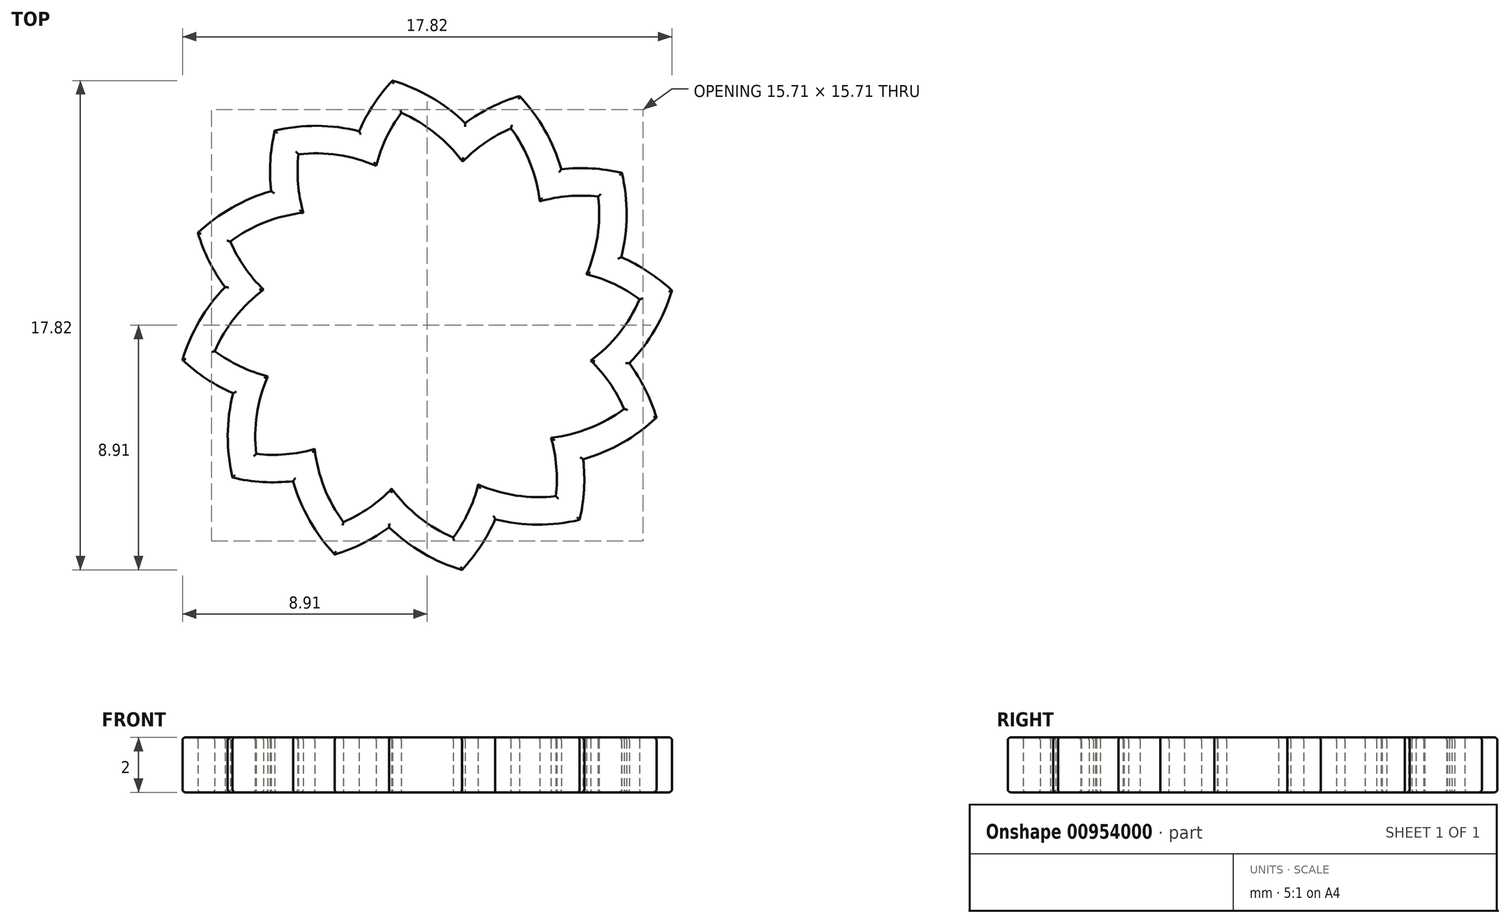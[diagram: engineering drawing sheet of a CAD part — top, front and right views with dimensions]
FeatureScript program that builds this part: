
annotation { "Feature Type Name" : "Feature", "Feature Type Description" : "" }
export const myFeature = defineFeature(function(context is Context, id is Id, definition is map)
    precondition{}
    {
        {
            var Q0;
            Q0=qCreatedBy(makeId("Top.planeOp"),FACE);
            var sketch = newSketch(context, id + "F0", { "sketchPlane" : qUnion([Q0])});
            skCircle(sketch, "E0", {"center": v(0, 0) * mm, "radius": 2.5 * mm});
            skSolve(sketch);
        }
        {
            var Q0;
            Q0=qCreatedBy(makeId("Top.planeOp"),FACE);
            var sketch = newSketch(context, id + "F1", { "sketchPlane" : qUnion([Q0])});
            skArc(sketch, "E1", {"start": v(-2.5, 0) * mm, "mid": v(-5.2, 3.04) * mm, "end": v(-5.55, 7.09) * mm});
            skArc(sketch, "E2", {"start": v(2.43, 0.6) * mm, "mid": v(0.03, 5.81) * mm, "end": v(-5.55, 7.09) * mm});
            skArc(sketch, "E3.1.0", {"start": v(1.8, 1.74) * mm, "mid": v(-2.88, 5.05) * mm, "end": v(-8.35, 3.36) * mm});
            skArc(sketch, "E3.1.1", {"start": v(-2.17, -1.25) * mm, "mid": v(-6.02, 0.04) * mm, "end": v(-8.35, 3.36) * mm});
            skArc(sketch, "E3.2.0", {"start": v(0.69, 2.4) * mm, "mid": v(-5.01, 2.93) * mm, "end": v(-8.91, -1.26) * mm});
            skArc(sketch, "E3.2.1", {"start": v(-1.25, -2.17) * mm, "mid": v(-5.23, -2.98) * mm, "end": v(-8.91, -1.26) * mm});
            skArc(sketch, "E3.3.0", {"start": v(-0.6, 2.43) * mm, "mid": v(-5.81, 0.03) * mm, "end": v(-7.09, -5.55) * mm});
            skArc(sketch, "E3.3.1", {"start": v(0, -2.5) * mm, "mid": v(-3.04, -5.2) * mm, "end": v(-7.09, -5.55) * mm});
            skArc(sketch, "E3.4.0", {"start": v(-1.74, 1.8) * mm, "mid": v(-5.05, -2.88) * mm, "end": v(-3.36, -8.35) * mm});
            skArc(sketch, "E3.4.1", {"start": v(1.25, -2.17) * mm, "mid": v(-0.04, -6.02) * mm, "end": v(-3.36, -8.35) * mm});
            skArc(sketch, "E3.5.0", {"start": v(-2.4, 0.69) * mm, "mid": v(-2.93, -5.01) * mm, "end": v(1.26, -8.91) * mm});
            skArc(sketch, "E3.5.1", {"start": v(2.17, -1.25) * mm, "mid": v(2.98, -5.23) * mm, "end": v(1.26, -8.91) * mm});
            skArc(sketch, "E3.6.0", {"start": v(-2.43, -0.6) * mm, "mid": v(-0.03, -5.81) * mm, "end": v(5.55, -7.09) * mm});
            skArc(sketch, "E3.6.1", {"start": v(2.5, 0) * mm, "mid": v(5.2, -3.04) * mm, "end": v(5.55, -7.09) * mm});
            skArc(sketch, "E3.7.0", {"start": v(-1.8, -1.74) * mm, "mid": v(2.88, -5.05) * mm, "end": v(8.35, -3.36) * mm});
            skArc(sketch, "E3.7.1", {"start": v(2.17, 1.25) * mm, "mid": v(6.02, -0.04) * mm, "end": v(8.35, -3.36) * mm});
            skArc(sketch, "E3.8.0", {"start": v(-0.69, -2.4) * mm, "mid": v(5.01, -2.93) * mm, "end": v(8.91, 1.26) * mm});
            skArc(sketch, "E3.8.1", {"start": v(1.25, 2.17) * mm, "mid": v(5.23, 2.98) * mm, "end": v(8.91, 1.26) * mm});
            skArc(sketch, "E3.9.0", {"start": v(0.6, -2.43) * mm, "mid": v(5.81, -0.03) * mm, "end": v(7.09, 5.55) * mm});
            skArc(sketch, "E3.9.1", {"start": v(0, 2.5) * mm, "mid": v(3.04, 5.2) * mm, "end": v(7.09, 5.55) * mm});
            skPoint(sketch, "E3.center", {"position": v(0, 0) * mm});
            skArc(sketch, "E4.0", {"start": v(0.19, 0.15) * mm, "mid": v(-3.52, 2.17) * mm, "end": v(-4.68, 6.22) * mm});
            skArc(sketch, "E4.1", {"start": v(1.25, 2.17) * mm, "mid": v(-0.96, 5.3) * mm, "end": v(-4.68, 6.22) * mm});
            skArc(sketch, "E5.1.0", {"start": v(0.09, 0.22) * mm, "mid": v(-4.13, 0.12) * mm, "end": v(-7.17, 3.05) * mm});
            skArc(sketch, "E5.1.1", {"start": v(0, 2.5) * mm, "mid": v(-3.48, 4.11) * mm, "end": v(-7.17, 3.05) * mm});
            skArc(sketch, "E5.2.0", {"start": v(-0.04, 0.24) * mm, "mid": v(-3.64, -1.96) * mm, "end": v(-7.73, -0.94) * mm});
            skArc(sketch, "E5.2.1", {"start": v(-1.25, 2.17) * mm, "mid": v(-5.07, 1.82) * mm, "end": v(-7.73, -0.94) * mm});
            skArc(sketch, "E5.3.0", {"start": v(-0.15, 0.19) * mm, "mid": v(-2.17, -3.52) * mm, "end": v(-6.22, -4.68) * mm});
            skArc(sketch, "E5.3.1", {"start": v(-2.17, 1.25) * mm, "mid": v(-5.3, -0.96) * mm, "end": v(-6.22, -4.68) * mm});
            skArc(sketch, "E5.4.0", {"start": v(-0.22, 0.09) * mm, "mid": v(-0.12, -4.13) * mm, "end": v(-3.05, -7.17) * mm});
            skArc(sketch, "E5.4.1", {"start": v(-2.5, 0) * mm, "mid": v(-4.11, -3.48) * mm, "end": v(-3.05, -7.17) * mm});
            skArc(sketch, "E5.5.0", {"start": v(-0.24, -0.04) * mm, "mid": v(1.96, -3.64) * mm, "end": v(0.94, -7.73) * mm});
            skArc(sketch, "E5.5.1", {"start": v(-2.17, -1.25) * mm, "mid": v(-1.82, -5.07) * mm, "end": v(0.94, -7.73) * mm});
            skArc(sketch, "E5.6.0", {"start": v(-0.19, -0.15) * mm, "mid": v(3.52, -2.17) * mm, "end": v(4.68, -6.22) * mm});
            skArc(sketch, "E5.6.1", {"start": v(-1.25, -2.17) * mm, "mid": v(0.96, -5.3) * mm, "end": v(4.68, -6.22) * mm});
            skArc(sketch, "E5.7.0", {"start": v(-0.09, -0.22) * mm, "mid": v(4.13, -0.12) * mm, "end": v(7.17, -3.05) * mm});
            skArc(sketch, "E5.7.1", {"start": v(0, -2.5) * mm, "mid": v(3.48, -4.11) * mm, "end": v(7.17, -3.05) * mm});
            skArc(sketch, "E5.8.0", {"start": v(0.04, -0.24) * mm, "mid": v(3.64, 1.96) * mm, "end": v(7.73, 0.94) * mm});
            skArc(sketch, "E5.8.1", {"start": v(1.25, -2.17) * mm, "mid": v(5.07, -1.82) * mm, "end": v(7.73, 0.94) * mm});
            skArc(sketch, "E5.9.0", {"start": v(0.15, -0.19) * mm, "mid": v(2.17, 3.52) * mm, "end": v(6.22, 4.68) * mm});
            skArc(sketch, "E5.9.1", {"start": v(2.17, -1.25) * mm, "mid": v(5.3, 0.96) * mm, "end": v(6.22, 4.68) * mm});
            skCircle(sketch, "E6", {"center": v(0, 0) * mm, "radius": 2.5 * mm});
            skArc(sketch, "E7.4.10.0", {"start": v(2.5, 0) * mm, "mid": v(4.11, 3.48) * mm, "end": v(3.05, 7.17) * mm});
            skArc(sketch, "E7.5.10.0", {"start": v(0.22, -0.09) * mm, "mid": v(0.12, 4.13) * mm, "end": v(3.05, 7.17) * mm});
            skArc(sketch, "E7.4.11.0", {"start": v(2.17, 1.25) * mm, "mid": v(1.82, 5.07) * mm, "end": v(-0.94, 7.73) * mm});
            skArc(sketch, "E7.5.11.0", {"start": v(0.24, 0.04) * mm, "mid": v(-1.96, 3.64) * mm, "end": v(-0.94, 7.73) * mm});
            skArc(sketch, "E8.1.10.0", {"start": v(1.74, -1.8) * mm, "mid": v(5.05, 2.88) * mm, "end": v(3.36, 8.35) * mm});
            skArc(sketch, "E8.4.10.0", {"start": v(-1.25, 2.17) * mm, "mid": v(0.04, 6.02) * mm, "end": v(3.36, 8.35) * mm});
            skArc(sketch, "E8.1.11.0", {"start": v(2.4, -0.69) * mm, "mid": v(2.93, 5.01) * mm, "end": v(-1.26, 8.91) * mm});
            skArc(sketch, "E8.4.11.0", {"start": v(-2.17, 1.25) * mm, "mid": v(-2.98, 5.23) * mm, "end": v(-1.26, 8.91) * mm});
            skSolve(sketch);
        }
        {
            var Q0;
            Q0 = qSketchRegion(id + "F1", true);
            extrude(context, id + "F2", {"entities" : qUnion([Q0]), "depth" : 2 * mm, "offsetDistance" : 25 * mm});
        }
        {
            var Q0;
            Q0=makeQuery(id+"F2.opExtrude","CAP_FACE",FACE,{"disambiguationData":[OSD([sQuery(id+"F1.wireOp",EDGE,"E1"),sQuery(id+"F1.wireOp",EDGE,"E2"),sQuery(id+"F1.wireOp",EDGE,"E3.1.0"),sQuery(id+"F1.wireOp",EDGE,"E3.1.1"),sQuery(id+"F1.wireOp",EDGE,"E3.2.0"),sQuery(id+"F1.wireOp",EDGE,"E3.2.1"),sQuery(id+"F1.wireOp",EDGE,"E3.3.0"),sQuery(id+"F1.wireOp",EDGE,"E3.3.1"),sQuery(id+"F1.wireOp",EDGE,"E3.4.0"),sQuery(id+"F1.wireOp",EDGE,"E3.4.1"),sQuery(id+"F1.wireOp",EDGE,"E3.5.0"),sQuery(id+"F1.wireOp",EDGE,"E3.5.1"),sQuery(id+"F1.wireOp",EDGE,"E3.6.0"),sQuery(id+"F1.wireOp",EDGE,"E3.6.1"),sQuery(id+"F1.wireOp",EDGE,"E3.7.0"),sQuery(id+"F1.wireOp",EDGE,"E3.7.1"),sQuery(id+"F1.wireOp",EDGE,"E3.8.0"),sQuery(id+"F1.wireOp",EDGE,"E3.8.1"),sQuery(id+"F1.wireOp",EDGE,"E3.9.0"),sQuery(id+"F1.wireOp",EDGE,"E3.9.1"),sQuery(id+"F1.wireOp",EDGE,"E4.0"),sQuery(id+"F1.wireOp",EDGE,"E4.1"),sQuery(id+"F1.wireOp",EDGE,"E5.1.0"),sQuery(id+"F1.wireOp",EDGE,"E5.1.1"),sQuery(id+"F1.wireOp",EDGE,"E5.2.0"),sQuery(id+"F1.wireOp",EDGE,"E5.2.1"),sQuery(id+"F1.wireOp",EDGE,"E5.3.0"),sQuery(id+"F1.wireOp",EDGE,"E5.3.1"),sQuery(id+"F1.wireOp",EDGE,"E5.4.0"),sQuery(id+"F1.wireOp",EDGE,"E5.4.1"),sQuery(id+"F1.wireOp",EDGE,"E5.5.0"),sQuery(id+"F1.wireOp",EDGE,"E5.5.1"),sQuery(id+"F1.wireOp",EDGE,"E5.6.0"),sQuery(id+"F1.wireOp",EDGE,"E5.6.1"),sQuery(id+"F1.wireOp",EDGE,"E5.7.0"),sQuery(id+"F1.wireOp",EDGE,"E5.7.1"),sQuery(id+"F1.wireOp",EDGE,"E5.8.0"),sQuery(id+"F1.wireOp",EDGE,"E5.8.1"),sQuery(id+"F1.wireOp",EDGE,"E5.9.0"),sQuery(id+"F1.wireOp",EDGE,"E5.9.1"),sQuery(id+"F1.wireOp",EDGE,"E6")])],"isStart":false});
            var Q1;
            Q1=makeQuery(id+"F2.opExtrude","CAP_FACE",FACE,{"disambiguationData":[OSD([sQuery(id+"F1.wireOp",EDGE,"E1"),sQuery(id+"F1.wireOp",EDGE,"E2"),sQuery(id+"F1.wireOp",EDGE,"E3.1.0"),sQuery(id+"F1.wireOp",EDGE,"E3.1.1"),sQuery(id+"F1.wireOp",EDGE,"E3.2.0"),sQuery(id+"F1.wireOp",EDGE,"E3.2.1"),sQuery(id+"F1.wireOp",EDGE,"E3.3.0"),sQuery(id+"F1.wireOp",EDGE,"E3.3.1"),sQuery(id+"F1.wireOp",EDGE,"E3.4.0"),sQuery(id+"F1.wireOp",EDGE,"E3.4.1"),sQuery(id+"F1.wireOp",EDGE,"E3.5.0"),sQuery(id+"F1.wireOp",EDGE,"E3.5.1"),sQuery(id+"F1.wireOp",EDGE,"E3.6.0"),sQuery(id+"F1.wireOp",EDGE,"E3.6.1"),sQuery(id+"F1.wireOp",EDGE,"E3.7.0"),sQuery(id+"F1.wireOp",EDGE,"E3.7.1"),sQuery(id+"F1.wireOp",EDGE,"E3.8.0"),sQuery(id+"F1.wireOp",EDGE,"E3.8.1"),sQuery(id+"F1.wireOp",EDGE,"E3.9.0"),sQuery(id+"F1.wireOp",EDGE,"E3.9.1"),sQuery(id+"F1.wireOp",EDGE,"E4.0"),sQuery(id+"F1.wireOp",EDGE,"E4.1"),sQuery(id+"F1.wireOp",EDGE,"E5.1.0"),sQuery(id+"F1.wireOp",EDGE,"E5.1.1"),sQuery(id+"F1.wireOp",EDGE,"E5.2.0"),sQuery(id+"F1.wireOp",EDGE,"E5.2.1"),sQuery(id+"F1.wireOp",EDGE,"E5.3.0"),sQuery(id+"F1.wireOp",EDGE,"E5.3.1"),sQuery(id+"F1.wireOp",EDGE,"E5.4.0"),sQuery(id+"F1.wireOp",EDGE,"E5.4.1"),sQuery(id+"F1.wireOp",EDGE,"E5.5.0"),sQuery(id+"F1.wireOp",EDGE,"E5.5.1"),sQuery(id+"F1.wireOp",EDGE,"E5.6.0"),sQuery(id+"F1.wireOp",EDGE,"E5.6.1"),sQuery(id+"F1.wireOp",EDGE,"E5.7.0"),sQuery(id+"F1.wireOp",EDGE,"E5.7.1"),sQuery(id+"F1.wireOp",EDGE,"E5.8.0"),sQuery(id+"F1.wireOp",EDGE,"E5.8.1"),sQuery(id+"F1.wireOp",EDGE,"E5.9.0"),sQuery(id+"F1.wireOp",EDGE,"E5.9.1"),sQuery(id+"F1.wireOp",EDGE,"E6")])],"isStart":true});
            fillet(context, id + "F3", {"entities" : qUnion([Q0, Q1]), "radius" : .1 * mm, "tangentPropagation" : true, "allowEdgeOverflow" : false});
        }
    });
